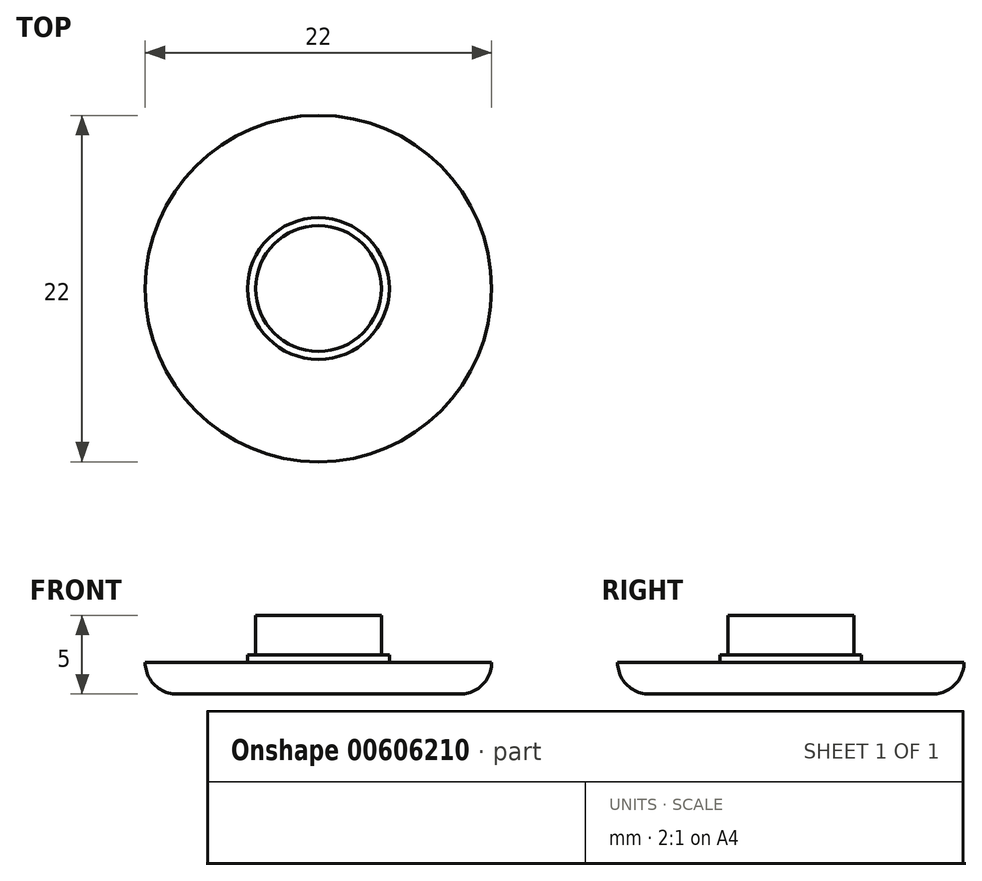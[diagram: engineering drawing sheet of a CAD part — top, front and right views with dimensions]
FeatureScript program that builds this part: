
annotation { "Feature Type Name" : "Feature", "Feature Type Description" : "" }
export const myFeature = defineFeature(function(context is Context, id is Id, definition is map)
    precondition{}
    {
        {
            var Q0;
            Q0=qCreatedBy(makeId("Top.planeOp"),FACE);
            var sketch = newSketch(context, id + "F0", { "sketchPlane" : qUnion([Q0])});
            skCircle(sketch, "E0", {"center": v(-124.76, 13.61) * mm, "radius": 11 * mm});
            skSolve(sketch);
        }
        {
            var Q0;
            Q0=makeQuery(id+"F0.imprint","IMPRINT",FACE,{"disambiguationData":[TD([[makeQuery(id+"F0.imprint","IMPRINT",EDGE,{"derivedFrom":sQuery(id+"F0.wireOp",EDGE,"E0")}),1.0]])]});
            extrude(context, id + "F1", {"entities" : qUnion([Q0]), "depth" : 2 * mm, "offsetDistance" : 25 * mm});
        }
        {
            var Q0;
            Q0=makeQuery(id+"F1.opExtrude","CAP_FACE",FACE,{"disambiguationData":[OSD([sQuery(id+"F0.wireOp",EDGE,"E0")])],"isStart":false});
            var sketch = newSketch(context, id + "F2", { "sketchPlane" : qUnion([Q0])});
            skCircle(sketch, "E1", {"center": v(-124.76, 13.61) * mm, "radius": 4.5 * mm});
            skSolve(sketch);
        }
        {
            var Q0;
            Q0=makeQuery(id+"F2.imprint","IMPRINT",FACE,{"disambiguationData":[TD([[makeQuery(id+"F2.imprint","IMPRINT",EDGE,{"derivedFrom":sQuery(id+"F2.wireOp",EDGE,"E1")}),1.0]])]});
            extrude(context, id + "F3", {"entities" : qUnion([Q0]), "operationType" : NewBodyOperationType.ADD, "depth" : 0.5 * mm, "offsetDistance" : 25 * mm});
        }
        {
            var Q0;
            Q0=makeQuery(id+"F3.opExtrude","CAP_FACE",FACE,{"disambiguationData":[OSD([sQuery(id+"F2.wireOp",EDGE,"E1")])],"isStart":false});
            var sketch = newSketch(context, id + "F4", { "sketchPlane" : qUnion([Q0])});
            skCircle(sketch, "E2", {"center": v(-124.76, 13.61) * mm, "radius": 4 * mm});
            skSolve(sketch);
        }
        {
            var Q0;
            Q0=makeQuery(id+"F4.imprint","IMPRINT",FACE,{"disambiguationData":[TD([[makeQuery(id+"F4.imprint","IMPRINT",EDGE,{"derivedFrom":sQuery(id+"F4.wireOp",EDGE,"E2")}),1.0]])]});
            extrude(context, id + "F5", {"entities" : qUnion([Q0]), "operationType" : NewBodyOperationType.ADD, "depth" : 2.5 * mm, "offsetDistance" : 25 * mm});
        }
        {
            var Q0;
            Q0=makeQuery(id+"F1.opExtrude","CAP_EDGE",EDGE,{"disambiguationData":[OSD([sQuery(id+"F0.wireOp",EDGE,"E0")])],"isStart":true});
            var Q1;
            Q1=makeQuery(id+"F3.opExtrude","CAP_EDGE",EDGE,{"disambiguationData":[OSD([sQuery(id+"F2.wireOp",EDGE,"E1")])],"isStart":true});
            fillet(context, id + "F6", {"entities" : qUnion([Q0, Q1]), "radius" : 2 * mm, "tangentPropagation" : true, "allowEdgeOverflow" : false});
        }
    });
